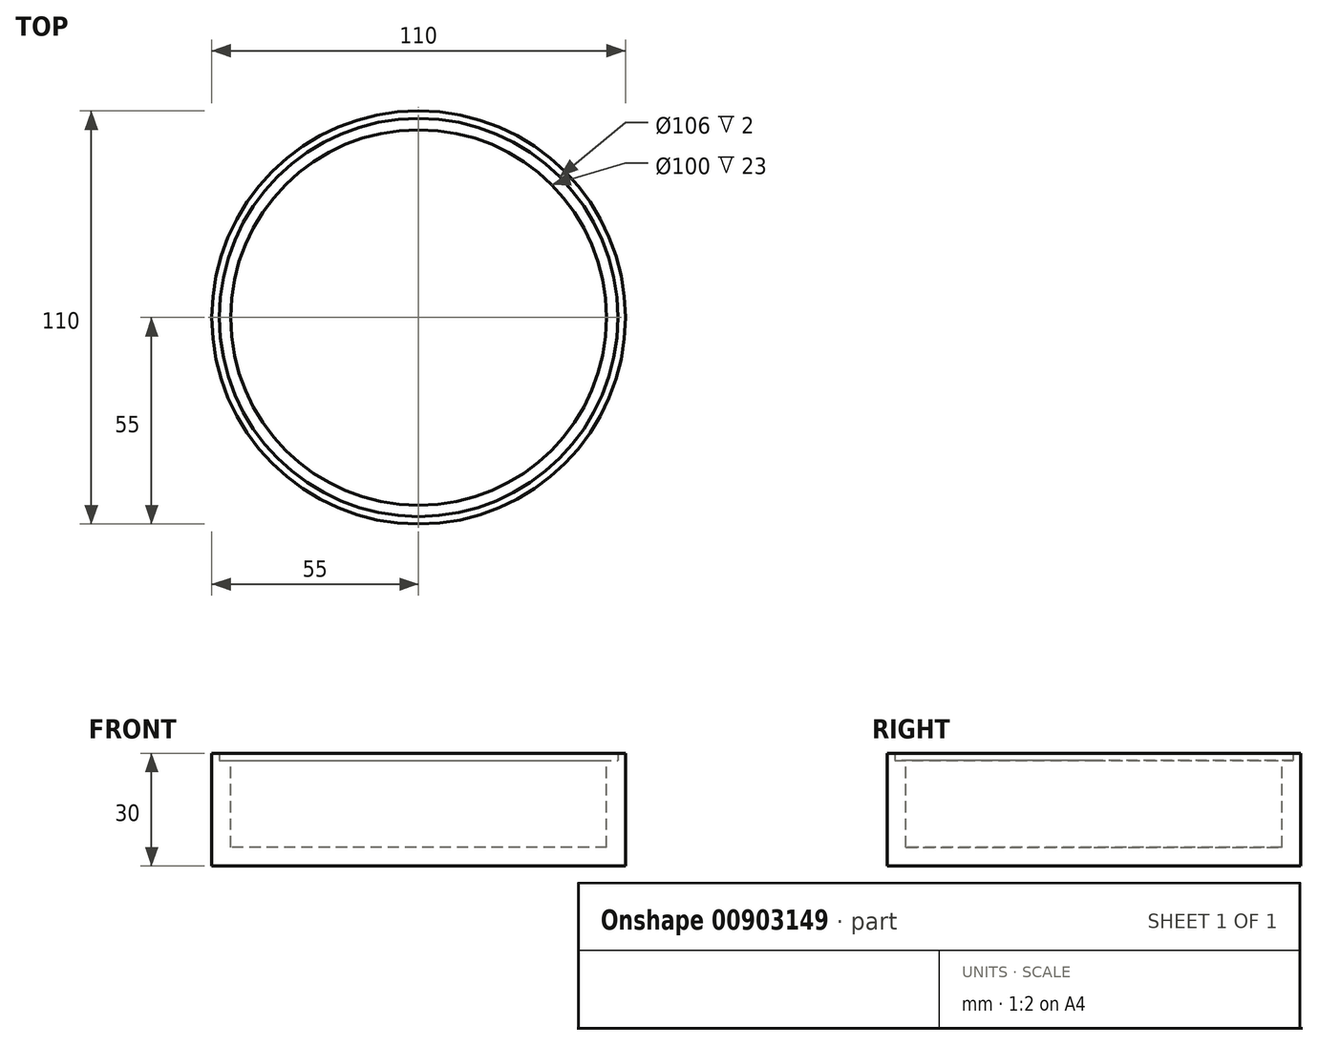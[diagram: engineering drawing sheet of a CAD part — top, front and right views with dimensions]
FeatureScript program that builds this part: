
annotation { "Feature Type Name" : "Feature", "Feature Type Description" : "" }
export const myFeature = defineFeature(function(context is Context, id is Id, definition is map)
    precondition{}
    {
        {
            var Q0;
            Q0=qCreatedBy(makeId("Front.planeOp"),FACE);
            var sketch = newSketch(context, id + "F0", { "sketchPlane" : qUnion([Q0])});
            skLineSegment(sketch, "E0", {"start": v(0, 0) * mm, "end": v(55, 0) * mm});
            skLineSegment(sketch, "E1", {"start": v(55, 0) * mm, "end": v(55, 30) * mm});
            skLineSegment(sketch, "E2", {"start": v(55, 30) * mm, "end": v(50, 30) * mm});
            skLineSegment(sketch, "E3", {"start": v(50, 30) * mm, "end": v(50, 5) * mm});
            skLineSegment(sketch, "E4", {"start": v(50, 5) * mm, "end": v(0, 5) * mm});
            skLineSegment(sketch, "E5", {"start": v(0, 5) * mm, "end": v(0, 0) * mm});
            skLineSegment(sketch, "E6", {"start": v(50, 28) * mm, "end": v(53, 28) * mm});
            skLineSegment(sketch, "E7", {"start": v(53, 28) * mm, "end": v(53, 30) * mm});
            skPoint(sketch, "E7.endSnap0", {"position": v(52.5, 30) * mm});
            skLineSegment(sketch, "E8", {"start": v(53, 30) * mm, "end": v(50, 30) * mm});
            skSolve(sketch);
        }
        {
            var Q0;
            Q0 = qSketchRegion(id + "F0", true);
            var Q1;
            Q1=sQuery(id+"F0.wireOp",EDGE,"E5");
            revolve(context, id + "F1", {"surfaceOperationType" : NewSurfaceOperationType.NEW, "entities" : qUnion([Q0]), "axis" : qUnion([Q1]), "revolveType" : RevolveType.FULL});
        }
        {
            var Q0;
            {var subQ2=sQuery(id+"F0.wireOp",EDGE,"E6");Q0=makeQuery(id+"F0.imprint","IMPRINT",FACE,{"disambiguationData":[TD([[makeQuery(id+"F0.imprint","IMPRINT",EDGE,{"derivedFrom":subQ2}),1.0]])]});}
            var Q1;
            Q1=sQuery(id+"F0.wireOp",EDGE,"E5");
            revolve(context, id + "F2", {"operationType" : NewBodyOperationType.REMOVE, "surfaceOperationType" : NewSurfaceOperationType.NEW, "entities" : qUnion([Q0]), "axis" : qUnion([Q1]), "revolveType" : RevolveType.FULL, "oppositeDirection" : true});
        }
    });
